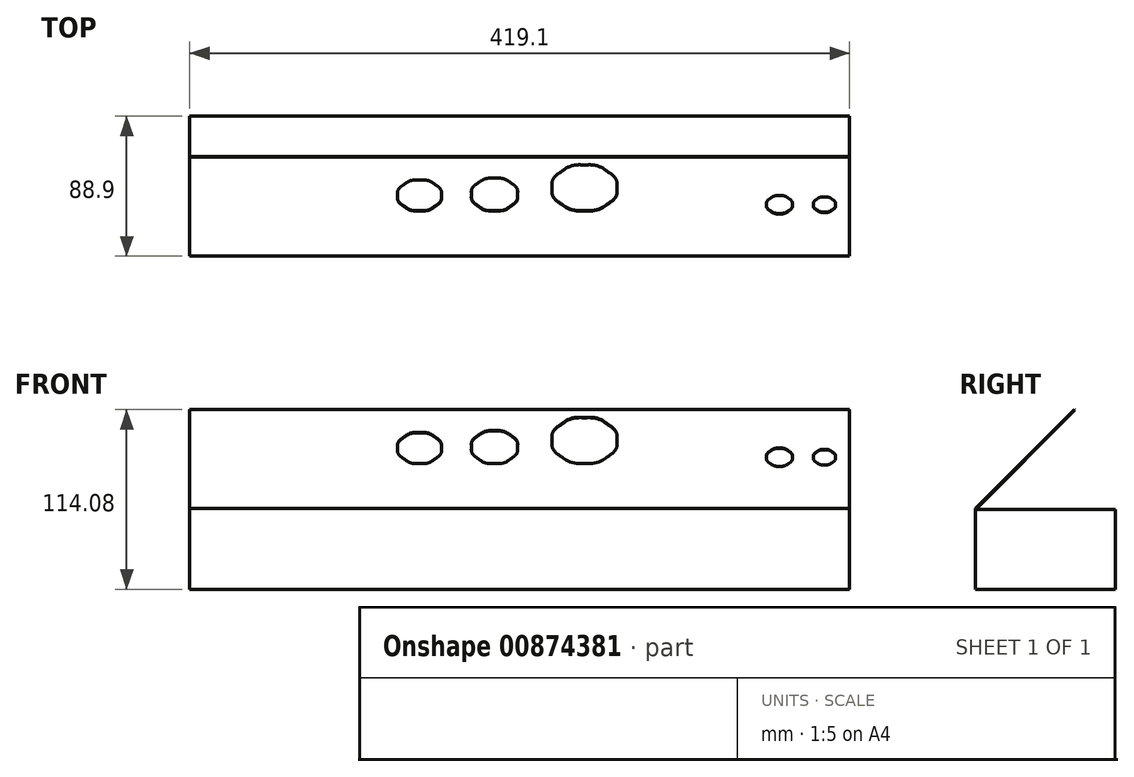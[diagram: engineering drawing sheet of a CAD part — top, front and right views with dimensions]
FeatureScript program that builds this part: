
annotation { "Feature Type Name" : "Feature", "Feature Type Description" : "" }
export const myFeature = defineFeature(function(context is Context, id is Id, definition is map)
    precondition{}
    {
        {
            var Q0;
            Q0=qCreatedBy(makeId("Right.planeOp"),FACE);
            var sketch = newSketch(context, id + "F0", { "sketchPlane" : qUnion([Q0])});
            skLineSegment(sketch, "E0.bottom", {"start": v(0, 0) * mm, "end": v(-88.9, 0) * mm});
            skLineSegment(sketch, "E0.top", {"start": v(0, 50.8) * mm, "end": v(-88.5, 50.8) * mm});
            skLineSegment(sketch, "E0.left", {"start": v(0, 0) * mm, "end": v(0, 50.8) * mm});
            skLineSegment(sketch, "E0.right", {"start": v(-88.9, 0) * mm, "end": v(-88.9, 51.22) * mm});
            skLineSegment(sketch, "E1", {"start": v(-88.9, 51.22) * mm, "end": v(-26.04, 114.08) * mm});
            skLineSegment(sketch, "E2", {"start": v(-26.04, 114.08) * mm, "end": v(-25.75, 113.8) * mm});
            skLineSegment(sketch, "E3", {"start": v(-25.75, 113.8) * mm, "end": v(-88.5, 51.05) * mm});
            skLineSegment(sketch, "E4", {"start": v(-88.5, 50.8) * mm, "end": v(-88.5, 51.05) * mm});
            skLineSegment(sketch, "E5", {"start": v(-88.5, 50.8) * mm, "end": v(-88.9, 50.8) * mm, "construction": true});
            skSolve(sketch);
        }
        {
            var Q0;
            Q0=qSketchRegion(id+"F0",true);
            extrude(context, id + "F1", {"entities" : qUnion([Q0]), "endBound" : BoundingType.SYMMETRIC, "depth" : 419.1 * mm, "offsetDistance" : 25.4 * mm});
        }
        {
            var Q0;
            Q0=makeQuery(id+"F1.opExtrude","SWEPT_FACE",FACE,{"disambiguationData":[OSD([sQuery(id+"F0.wireOp",EDGE,"E1")])]});
            var sketch = newSketch(context, id + "F2", { "sketchPlane" : qUnion([Q0])});
            skLineSegment(sketch, "E6", {"start": v(106.2, 39.42) * mm, "end": v(106.2, 34.66) * mm});
            skLineSegment(sketch, "E7", {"start": v(106.2, 25.13) * mm, "end": v(106.2, 20.37) * mm});
            skLineSegment(sketch, "E8", {"start": v(106.2, 20.37) * mm, "end": v(110.97, 20.37) * mm});
            skLineSegment(sketch, "E9", {"start": v(110.97, 39.42) * mm, "end": v(106.2, 39.42) * mm});
            skLineSegment(sketch, "E10", {"start": v(-209.7, -27.26) * mm, "end": v(-209.7, 60.85) * mm, "construction": true});
            skLineSegment(sketch, "E11", {"start": v(126.84, 20.37) * mm, "end": v(131.6, 20.37) * mm});
            skLineSegment(sketch, "E12", {"start": v(131.6, 39.42) * mm, "end": v(126.84, 39.42) * mm});
            skLineSegment(sketch, "E13", {"start": v(131.6, 20.37) * mm, "end": v(131.6, 25.13) * mm});
            skLineSegment(sketch, "E14", {"start": v(131.6, 34.66) * mm, "end": v(131.6, 39.42) * mm});
            skLineSegment(sketch, "E15", {"start": v(209.4, -27.26) * mm, "end": v(209.4, 60.85) * mm, "construction": true});
            skLineSegment(sketch, "E16", {"start": v(209.4, -27.26) * mm, "end": v(-209.7, -27.26) * mm, "construction": true});
            skLineSegment(sketch, "E17", {"start": v(-209.7, 60.85) * mm, "end": v(209.4, 60.85) * mm, "construction": true});
            skFitSpline(sketch, "E18", {"points": [v(-63.66, 41.8) * mm, v(-67.3, 41.8) * mm, v(-70.91, 40.3) * mm, v(-73.48, 37.73) * mm]});
            skFitSpline(sketch, "E19", {"points": [v(-73.48, 37.73) * mm, v(-76.05, 35.16) * mm, v(-77.55, 31.55) * mm, v(-77.55, 27.91) * mm, v(-77.55, 24.27) * mm, v(-76.05, 20.66) * mm, v(-73.48, 18.09) * mm]});
            skFitSpline(sketch, "E20", {"points": [v(-73.48, 18.09) * mm, v(-70.91, 15.52) * mm, v(-67.3, 14.02) * mm, v(-63.66, 14.02) * mm, v(-60.02, 14.02) * mm, v(-56.4, 15.52) * mm, v(-53.84, 18.09) * mm]});
            skFitSpline(sketch, "E21", {"points": [v(-53.84, 18.09) * mm, v(-51.27, 20.66) * mm, v(-49.77, 24.27) * mm, v(-49.77, 27.91) * mm, v(-49.77, 31.55) * mm, v(-51.27, 35.16) * mm, v(-53.84, 37.73) * mm]});
            skFitSpline(sketch, "E22", {"points": [v(-53.84, 37.73) * mm, v(-56.4, 40.3) * mm, v(-60.02, 41.8) * mm, v(-63.66, 41.8) * mm]});
            skFitSpline(sketch, "E23", {"points": [v(-16.03, 43.39) * mm, v(-19.88, 43.39) * mm, v(-23.7, 41.8) * mm, v(-26.42, 39.09) * mm]});
            skFitSpline(sketch, "E24", {"points": [v(-26.42, 39.09) * mm, v(-29.14, 36.37) * mm, v(-30.72, 32.55) * mm, v(-30.72, 28.7) * mm, v(-30.72, 24.86) * mm, v(-29.14, 21.04) * mm, v(-26.42, 18.32) * mm]});
            skFitSpline(sketch, "E25", {"points": [v(-26.42, 18.32) * mm, v(-23.7, 15.6) * mm, v(-19.88, 14.02) * mm, v(-16.03, 14.02) * mm, v(-12.2, 14.02) * mm, v(-8.37, 15.6) * mm, v(-5.65, 18.32) * mm]});
            skFitSpline(sketch, "E26", {"points": [v(-5.65, 18.32) * mm, v(-2.93, 21.04) * mm, v(-1.35, 24.86) * mm, v(-1.35, 28.7) * mm, v(-1.35, 32.55) * mm, v(-2.93, 36.37) * mm, v(-5.65, 39.09) * mm]});
            skFitSpline(sketch, "E27", {"points": [v(-5.65, 39.09) * mm, v(-8.37, 41.8) * mm, v(-12.2, 43.39) * mm, v(-16.03, 43.39) * mm]});
            skFitSpline(sketch, "E28", {"points": [v(41.12, 55.3) * mm, v(35.71, 55.3) * mm, v(30.34, 53.07) * mm, v(26.52, 49.25) * mm]});
            skFitSpline(sketch, "E29", {"points": [v(26.52, 49.25) * mm, v(22.7, 45.43) * mm, v(20.48, 40.06) * mm, v(20.48, 34.66) * mm, v(20.48, 29.25) * mm, v(22.7, 23.88) * mm, v(26.52, 20.06) * mm]});
            skFitSpline(sketch, "E30", {"points": [v(26.52, 20.06) * mm, v(30.34, 16.24) * mm, v(35.71, 14.02) * mm, v(41.12, 14.02) * mm, v(46.52, 14.02) * mm, v(51.89, 16.24) * mm, v(55.7, 20.06) * mm]});
            skFitSpline(sketch, "E31", {"points": [v(55.7, 20.06) * mm, v(59.53, 23.88) * mm, v(61.75, 29.25) * mm, v(61.75, 34.66) * mm, v(61.75, 40.06) * mm, v(59.53, 45.43) * mm, v(55.7, 49.25) * mm]});
            skFitSpline(sketch, "E32", {"points": [v(55.7, 49.25) * mm, v(51.89, 53.07) * mm, v(46.52, 55.3) * mm, v(41.12, 55.3) * mm]});
            skFitSpline(sketch, "E33", {"points": [v(193.52, 26.52) * mm, v(191.7, 26.52) * mm, v(189.9, 25.77) * mm, v(188.6, 24.49) * mm]});
            skFitSpline(sketch, "E34", {"points": [v(188.6, 24.49) * mm, v(187.32, 23.2) * mm, v(186.57, 21.4) * mm, v(186.57, 19.58) * mm, v(186.57, 17.76) * mm, v(187.32, 15.95) * mm, v(188.6, 14.67) * mm]});
            skFitSpline(sketch, "E35", {"points": [v(188.6, 14.67) * mm, v(189.9, 13.38) * mm, v(191.7, 12.63) * mm, v(193.52, 12.63) * mm, v(195.33, 12.63) * mm, v(197.14, 13.38) * mm, v(198.43, 14.67) * mm]});
            skFitSpline(sketch, "E36", {"points": [v(198.43, 14.67) * mm, v(199.71, 15.95) * mm, v(200.46, 17.76) * mm, v(200.46, 19.58) * mm, v(200.46, 21.4) * mm, v(199.71, 23.2) * mm, v(198.43, 24.49) * mm]});
            skFitSpline(sketch, "E37", {"points": [v(198.43, 24.49) * mm, v(197.14, 25.77) * mm, v(195.33, 26.52) * mm, v(193.52, 26.52) * mm]});
            skFitSpline(sketch, "E38", {"points": [v(164.94, 27.71) * mm, v(162.81, 27.71) * mm, v(160.7, 26.84) * mm, v(159.19, 25.33) * mm]});
            skFitSpline(sketch, "E39", {"points": [v(159.19, 25.33) * mm, v(157.68, 23.82) * mm, v(156.8, 21.7) * mm, v(156.8, 19.58) * mm, v(156.8, 17.45) * mm, v(157.68, 15.33) * mm, v(159.19, 13.82) * mm]});
            skFitSpline(sketch, "E40", {"points": [v(159.19, 13.82) * mm, v(160.7, 12.32) * mm, v(162.81, 11.44) * mm, v(164.94, 11.44) * mm, v(167.07, 11.44) * mm, v(169.19, 12.32) * mm, v(170.7, 13.82) * mm]});
            skFitSpline(sketch, "E41", {"points": [v(170.7, 13.82) * mm, v(172.2, 15.33) * mm, v(173.08, 17.45) * mm, v(173.08, 19.58) * mm, v(173.08, 21.7) * mm, v(172.2, 23.82) * mm, v(170.7, 25.33) * mm]});
            skFitSpline(sketch, "E42", {"points": [v(170.7, 25.33) * mm, v(169.19, 26.84) * mm, v(167.07, 27.71) * mm, v(164.94, 27.71) * mm]});
            skSolve(sketch);
        }
        {
            var Q0;
            Q0=qSketchRegion(id+"F2",true);
            var Q1;
            Q1=makeQuery(id+"F1.opExtrude","SWEPT_FACE",FACE,{"disambiguationData":[OSD([sQuery(id+"F0.wireOp",EDGE,"E3")])]});
            extrude(context, id + "F3", {"entities" : qUnion([Q0]), "operationType" : NewBodyOperationType.REMOVE, "endBound" : BoundingType.UP_TO_SURFACE, "oppositeDirection" : true, "depth" : 25.4 * mm, "endBoundEntityFace" : qUnion([Q1]), "offsetDistance" : 25.4 * mm});
        }
    });
